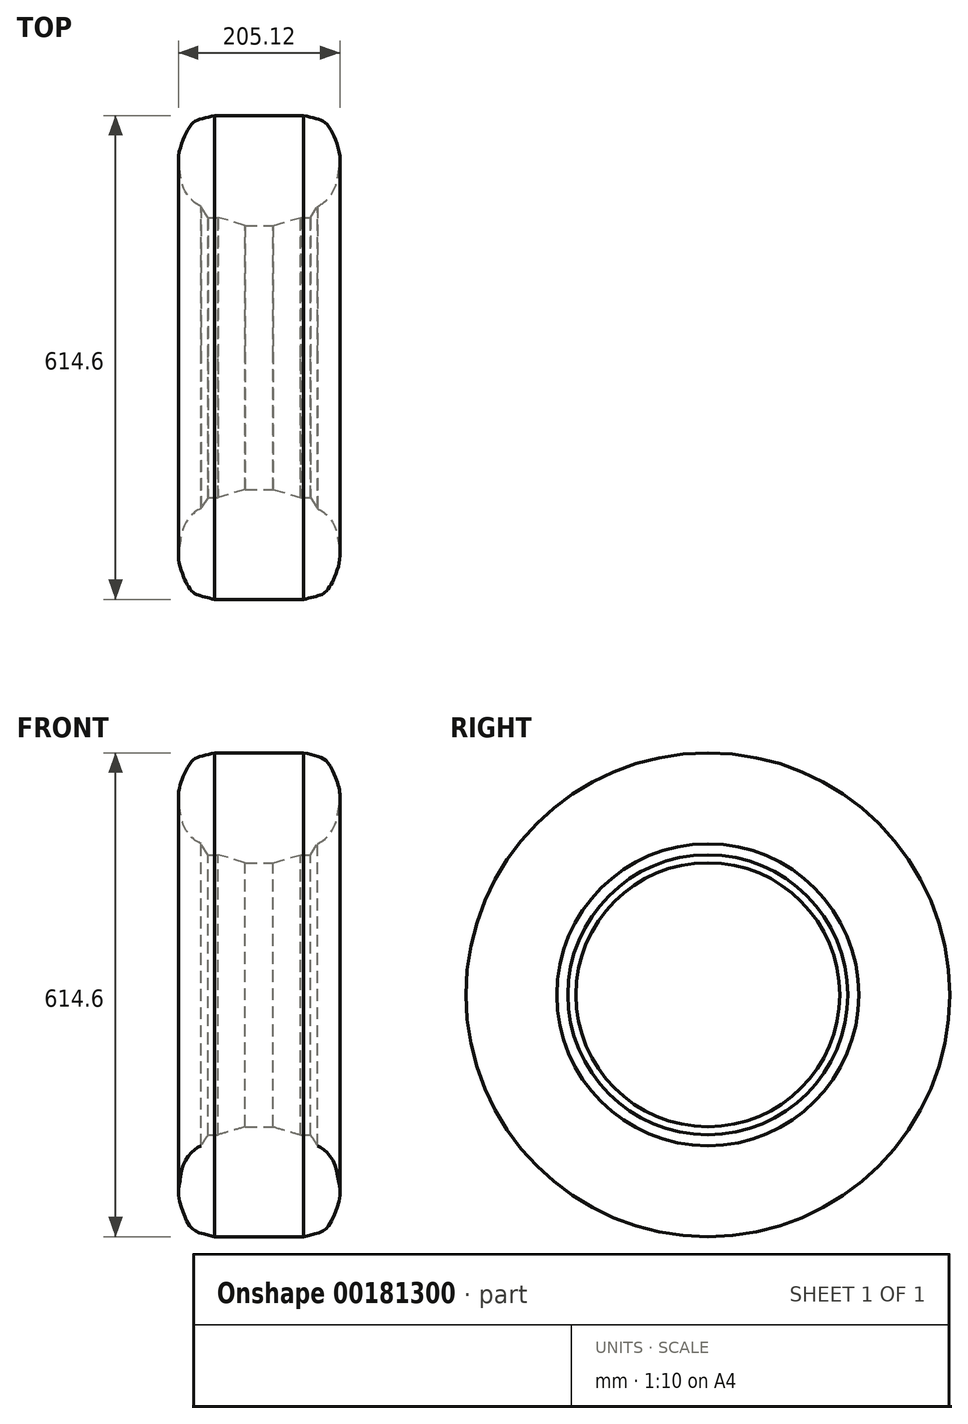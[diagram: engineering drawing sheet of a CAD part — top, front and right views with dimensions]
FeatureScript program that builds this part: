
annotation { "Feature Type Name" : "Feature", "Feature Type Description" : "" }
export const myFeature = defineFeature(function(context is Context, id is Id, definition is map)
    precondition{}
    {
        {
            var Q0;
            Q0=qCreatedBy(makeId("Front.planeOp"),FACE);
            var sketch = newSketch(context, id + "F0", { "sketchPlane" : qUnion([Q0])});
            skLineSegment(sketch, "E0", {"start": v(52.45, 0) * mm, "end": v(64.93, 0) * mm});
            skLineSegment(sketch, "E1", {"start": v(0, -10.13) * mm, "end": v(17.76, -10.13) * mm});
            skLineSegment(sketch, "E2", {"start": v(17.76, -10.13) * mm, "end": v(52.45, 0) * mm});
            skLineSegment(sketch, "E3", {"start": v(64.93, 0) * mm, "end": v(74.1, 14.01) * mm});
            skFitSpline(sketch, "E4", {"points": [v(74.1, 14.01) * mm, v(84.27, 20.82) * mm, v(96.04, 37.57) * mm, v(101.02, 60.21) * mm, v(101.93, 81.5) * mm, v(88.34, 115.46) * mm, v(78.38, 123.6) * mm, v(56.65, 129.5) * mm], "startDerivative": vector(91.95, 51.03) * mm, "endDerivative": vector(-163.24, 36.92) * mm});
            skLineSegment(sketch, "E5", {"start": v(0, 129.5) * mm, "end": v(56.65, 129.5) * mm});
            skLineSegment(sketch, "E6.MirrorCS", {"start": v(0, -10.13) * mm, "end": v(-17.76, -10.13) * mm});
            skLineSegment(sketch, "E7.MirrorCS", {"start": v(-17.76, -10.13) * mm, "end": v(-52.45, 0) * mm});
            skLineSegment(sketch, "E8.MirrorCS", {"start": v(-52.45, 0) * mm, "end": v(-64.93, 0) * mm});
            skLineSegment(sketch, "E9.MirrorCS", {"start": v(-64.93, 0) * mm, "end": v(-74.1, 14.01) * mm});
            skLineSegment(sketch, "E10.MirrorCS", {"start": v(0, 129.5) * mm, "end": v(-56.65, 129.5) * mm});
            skFitSpline(sketch, "E11.MirrorCS", {"points": [v(-74.1, 14.01) * mm, v(-84.27, 20.82) * mm, v(-96.04, 37.57) * mm, v(-101.02, 60.21) * mm, v(-101.93, 81.5) * mm, v(-88.34, 115.46) * mm, v(-78.38, 123.6) * mm, v(-56.65, 129.5) * mm], "startDerivative": vector(-91.95, 51.03) * mm, "endDerivative": vector(163.24, 36.92) * mm});
            skLineSegment(sketch, "E12.0", {"start": v(0, -177.8) * mm, "end": v(-118.2, -177.8) * mm});
            skSolve(sketch);
        }
        {
            var Q0;
            Q0 = qSketchRegion(id + "F0", true);
            var Q1;
            Q1=sQuery(id+"F0.wireOp",EDGE,"E12.0");
            revolve(context, id + "F1", {"entities" : qUnion([Q0]), "axis" : qUnion([Q1]), "revolveType" : RevolveType.FULL});
        }
    });
